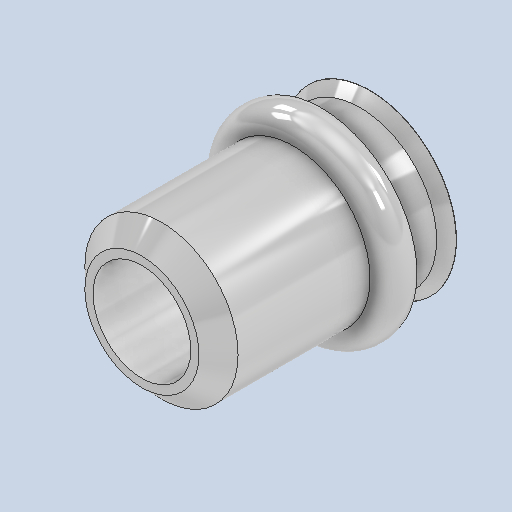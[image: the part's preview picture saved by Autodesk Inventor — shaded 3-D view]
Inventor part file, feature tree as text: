
AUTODESK INVENTOR PART (.ipt)
format: ipt  version: 2024.2 (Build 282272000, 272)  size: 207,360 bytes
history: native  units: mm
features: extrude x4, chamfer x2, projected_geometry x2, plane x1, sweep x1, sketch x1
ambient origin geometry x8: Origin, YZ Plane, XZ Plane, XY Plane, X Axis, Y Axis, Z Axis, Center Point
bodies: Solid1 (feature_tree)
feature tree (11):
  extrude  "Extrusion1"  Depth=7.0mm TaperAngle=0.0deg
  chamfer  "Chamfer1"  Distance=0.6mm Angle=45.0deg
  extrude  "Extrusion2"  Depth=7.0mm
  extrude  "Extrusion3"  TaperAngle=0.0deg  [1 undecoded]
  chamfer  "Chamfer2"  Distance=0.01mm
  extrude  "Extrusion4"  Depth=7.0mm
  plane  "Work Plane1"
  sweep  "Sweep1"
  projected_geometry  "Projected Loop1"
  projected_geometry  "Projected Loop2"
  sketch  "Sketch6"  dims[d0=4.7mm d1=7.0mm d2=0.0mm d3=0.6mm d4=2.0mm d5=45.0deg d6=3.0mm d7=0.0mm d8=0.0mm d9=0.01mm d10=0.0mm d11=5.3mm d12=0.3mm d13=2.0mm d14=45.0deg d15=0.0mm d16=0.0mm d17=-1.5mm d18=3.0mm d19=0.0mm d20=0.0mm]
note: 1 required parameter value undecoded (feature->parameter linkage not recoverable at this tier; creation-order binding heuristic only, values carry confidence <= 0.55)
